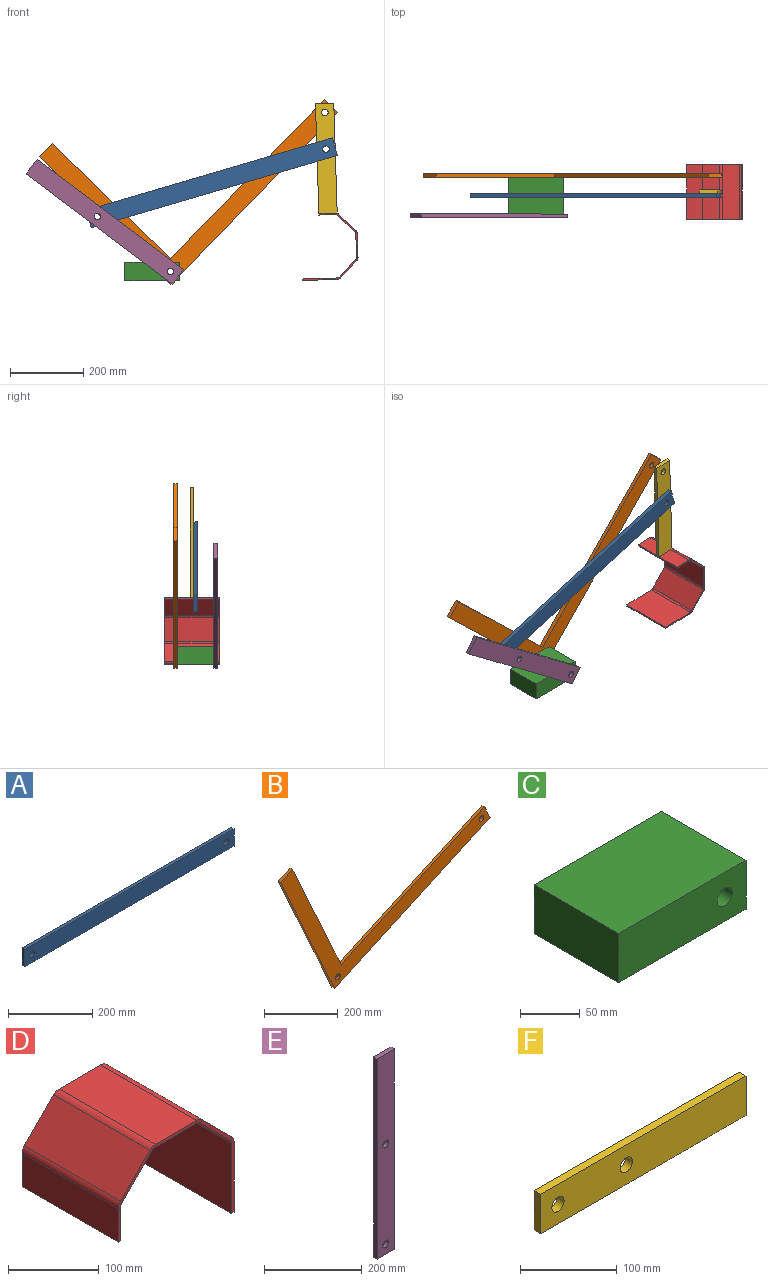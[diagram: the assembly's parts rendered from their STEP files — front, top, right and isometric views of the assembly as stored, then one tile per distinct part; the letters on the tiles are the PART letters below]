
ASSEMBLY  parts=6 mates=6
PART A: 8 faces, bbox 700x10x50 mm
  f0: plane 700x10mm, normal (0,0,-1), area 7000mm2, adj f1,f3,f6,f7
  f1: plane 50x10mm, normal (-1,0,0), area 500mm2, adj f0,f2,f6,f7
  f2: plane 700x10mm, normal (0,0,1), area 7000mm2, adj f1,f3,f6,f7
  f3: plane 50x10mm, normal (1,0,0), area 500mm2, adj f0,f2,f6,f7
  f4: cylinder r=9mm len=18mm, axis (0,-1,0), area 565.5mm2, adj f6,f7
  f5: cylinder r=9mm len=18mm, axis (0,-1,0), area 565.5mm2, adj f6,f7
  f6: plane 700x50mm, normal (0,1,0), area 34491.1mm2, adj f0,f1,f2,f3,f4,f5
  f7: plane 700x50mm, normal (0,-1,0), area 34491.1mm2, adj f0,f1,f2,f3,f4,f5
PART B: 10 faces, bbox 802.4x10x475.9 mm
  f0: plane 595.52x270.69mm, normal (0.41,0,-0.91), area 6541.5mm2, adj f1,f6,f8,f9
  f1: plane 455.18x206.9mm, normal (-0.91,0,-0.41), area 5000mm2, adj f0,f2,f8,f9
  f2: plane 45.52x20.69mm, normal (-0.41,0,0.91), area 500mm2, adj f1,f3,f8,f9
  f3: plane 409.67x186.21mm, normal (0.91,0,0.41), area 4500mm2, adj f2,f4,f8,f9
  f4: plane 550x250mm, normal (-0.41,0,0.91), area 6041.5mm2, adj f3,f6,f8,f9
  f5: cylinder r=9mm len=18mm, axis (0,-1,0), area 565.5mm2, adj f8,f9
  f6: plane 45.52x20.69mm, normal (0.91,0,0.41), area 500mm2, adj f0,f4,f8,f9
  f7: cylinder r=9mm len=18mm, axis (0,-1,0), area 565.5mm2, adj f8,f9
  f8: plane 802.42x475.87mm, normal (0,1,0), area 54698.7mm2, adj f0,f1,f2,f3,f4,f5,f6,f7
  f9: plane 802.42x475.87mm, normal (0,-1,0), area 54698.7mm2, adj f0,f1,f2,f3,f4,f5,f6,f7
PART C: 7 faces, bbox 150x100x50 mm
  f0: plane 100x50mm, normal (-1,0,0), area 5000mm2, adj f1,f3,f5,f6
  f1: plane 150x100mm, normal (0,0,-1), area 15000mm2, adj f0,f2,f5,f6
  f2: plane 100x50mm, normal (1,0,0), area 5000mm2, adj f1,f3,f5,f6
  f3: plane 150x100mm, normal (0,0,1), area 15000mm2, adj f0,f2,f5,f6
  f4: cylinder r=9mm len=100mm, axis (0,1,0), area 5654.9mm2, adj f5,f6
  f5: plane 150x50mm, normal (0,-1,0), area 7245.5mm2, adj f0,f1,f2,f3,f4
  f6: plane 150x50mm, normal (0,1,0), area 7245.5mm2, adj f0,f1,f2,f3,f4
PART D: 38 faces, bbox 181.1x150x153 mm
  f0: plane 45.03x4mm, normal (0,-1,0), area 180.1mm2, adj f2,f3,f4,f35
  f1: plane 45.03x4mm, normal (0,1,0), area 180.1mm2, adj f2,f3,f4,f34
  f2: plane 150x4mm, normal (0,0,-1), area 600mm2, adj f0,f1,f3,f4
  f3: plane 150x45.03mm, normal (-1,0,0), area 6754.4mm2, adj f0,f1,f2,f36
  f4: plane 150x45.03mm, normal (1,0,0), area 6754.4mm2, adj f0,f1,f2,f37
  f5: plane 48.83x48.83mm, normal (0,-1,0), area 260.2mm2, adj f7,f8,f31,f35
  f6: plane 48.83x48.83mm, normal (0,1,0), area 260.2mm2, adj f7,f8,f30,f34
  f7: plane 150x46mm, normal (-0.71,0,0.71), area 9758.8mm2, adj f5,f6,f32,f36
  f8: plane 150x46mm, normal (0.71,0,-0.71), area 9758.8mm2, adj f5,f6,f33,f37
  f9: plane 65.06x4mm, normal (0,-1,0), area 260.2mm2, adj f11,f12,f27,f31
  f10: plane 65.06x4mm, normal (0,1,0), area 260.2mm2, adj f11,f12,f26,f30
  f11: plane 150x65.06mm, normal (0,0,1), area 9758.8mm2, adj f9,f10,f28,f32
  f12: plane 150x65.06mm, normal (0,0,-1), area 9758.8mm2, adj f9,f10,f29,f33
  f13: plane 48.83x48.83mm, normal (0,-1,0), area 260.2mm2, adj f15,f16,f23,f27
  f14: plane 48.83x48.83mm, normal (0,1,0), area 260.2mm2, adj f15,f16,f22,f26
  f15: plane 150x46mm, normal (0.71,0,0.71), area 9758.8mm2, adj f13,f14,f24,f28
  f16: plane 150x46mm, normal (-0.71,0,-0.71), area 9758.8mm2, adj f13,f14,f25,f29
  f17: plane 95.03x4mm, normal (0,-1,0), area 380.1mm2, adj f18,f20,f21,f23
  f18: plane 150x4mm, normal (0,0,-1), area 600mm2, adj f17,f19,f20,f21
  f19: plane 95.03x4mm, normal (0,1,0), area 380.1mm2, adj f18,f20,f21,f22
  f20: plane 150x95.03mm, normal (1,0,0), area 14254.4mm2, adj f17,f18,f19,f24
  f21: plane 150x95.03mm, normal (-1,0,0), area 14254.4mm2, adj f17,f18,f19,f25
  f22: plane 8.49x6.34mm, normal (0,1,0), area 31.4mm2, adj f14,f19,f24,f25
  f23: plane 8.49x6.34mm, normal (0,-1,0), area 31.4mm2, adj f13,f17,f24,f25
  f24: cylinder r=12mm len=150mm, axis (0,1,0), area 1413.7mm2, adj f15,f20,f22,f23
  f25: cylinder r=8mm len=150mm, axis (0,1,0), area 942.5mm2, adj f16,f21,f22,f23
  f26: plane 8.49x6.34mm, normal (0,1,0), area 31.4mm2, adj f10,f14,f28,f29
  f27: plane 8.49x6.34mm, normal (0,-1,0), area 31.4mm2, adj f9,f13,f28,f29
  f28: cylinder r=12mm len=150mm, axis (0,1,0), area 1413.7mm2, adj f11,f15,f26,f27
  f29: cylinder r=8mm len=150mm, axis (0,1,0), area 942.5mm2, adj f12,f16,f26,f27
  f30: plane 8.49x6.34mm, normal (0,1,0), area 31.4mm2, adj f6,f10,f32,f33
  f31: plane 8.49x6.34mm, normal (0,-1,0), area 31.4mm2, adj f5,f9,f32,f33
  f32: cylinder r=12mm len=150mm, axis (0,1,0), area 1413.7mm2, adj f7,f11,f30,f31
  f33: cylinder r=8mm len=150mm, axis (0,1,0), area 942.5mm2, adj f8,f12,f30,f31
  f34: plane 8.49x6.34mm, normal (0,1,0), area 31.4mm2, adj f1,f6,f36,f37
  f35: plane 8.49x6.34mm, normal (0,-1,0), area 31.4mm2, adj f0,f5,f36,f37
  f36: cylinder r=12mm len=150mm, axis (0,1,0), area 1413.7mm2, adj f3,f7,f34,f35
  f37: cylinder r=8mm len=150mm, axis (0,1,0), area 942.5mm2, adj f4,f8,f34,f35
PART E: 8 faces, bbox 50x10x500 mm
  f0: plane 500x10mm, normal (-1,0,0), area 5000mm2, adj f1,f3,f6,f7
  f1: plane 50x10mm, normal (0,0,-1), area 500mm2, adj f0,f2,f6,f7
  f2: plane 500x10mm, normal (1,0,0), area 5000mm2, adj f1,f3,f6,f7
  f3: plane 50x10mm, normal (0,0,1), area 500mm2, adj f0,f2,f6,f7
  f4: cylinder r=9mm len=18mm, axis (0,1,0), area 565.5mm2, adj f6,f7
  f5: cylinder r=9mm len=18mm, axis (0,1,0), area 565.5mm2, adj f6,f7
  f6: plane 500x50mm, normal (0,-1,0), area 24491.1mm2, adj f0,f1,f2,f3,f4,f5
  f7: plane 500x50mm, normal (0,1,0), area 24491.1mm2, adj f0,f1,f2,f3,f4,f5
PART F: 8 faces, bbox 300x10x50 mm
  f0: plane 300x10mm, normal (0,0,-1), area 3000mm2, adj f1,f4,f6,f7
  f1: plane 50x10mm, normal (-1,0,0), area 500mm2, adj f0,f2,f6,f7
  f2: plane 300x10mm, normal (0,0,1), area 3000mm2, adj f1,f4,f6,f7
  f3: cylinder r=9mm len=18mm, axis (0,-1,0), area 565.5mm2, adj f6,f7
  f4: plane 50x10mm, normal (1,0,0), area 500mm2, adj f0,f2,f6,f7
  f5: cylinder r=9mm len=18mm, axis (0,-1,0), area 565.5mm2, adj f6,f7
  f6: plane 300x50mm, normal (0,1,0), area 14491.1mm2, adj f0,f1,f2,f3,f4,f5
  f7: plane 300x50mm, normal (0,-1,0), area 14491.1mm2, adj f0,f1,f2,f3,f4,f5
PLACE A rot(axis=(0,-1,0),16.4deg) t=(-117.14,45,-123.82)mm
PLACE B rot(axis=(0,-1,0),21.4deg) t=(17.76,0,-43.92)mm
PLACE C at identity fixed
PLACE D rot(axis=(0,1,0),88.2deg) t=(249.96,50,1124.76)mm
PLACE E rot(axis=(0,-1,0),53.1deg) t=(69.84,0,-89.92)mm
PLACE F rot(axis=(0,1,0),88.2deg) t=(249.96,45,1124.76)mm
MATE revolute C.f4 <-> E.f5  axis (0,1,0) through (125,-50,25)mm
MATE fastened F.f4 <-> D.f3  axis (0.03,0,-1) through (529.23,10,182.95)mm
MATE cylindrical B.f5 <-> F.f3  axis (0,-1,0) through (545.71,50,458.59)mm
MATE revolute A.f4 <-> F.f5  axis (0,1,0) through (548.81,5,358.64)mm
MATE revolute B.f7 <-> C.f4  axis (0,-1,0) through (125,50,25)mm
MATE revolute A.f5 <-> E.f4  axis (0,-1,0) through (-74.79,-5,175.27)mm
